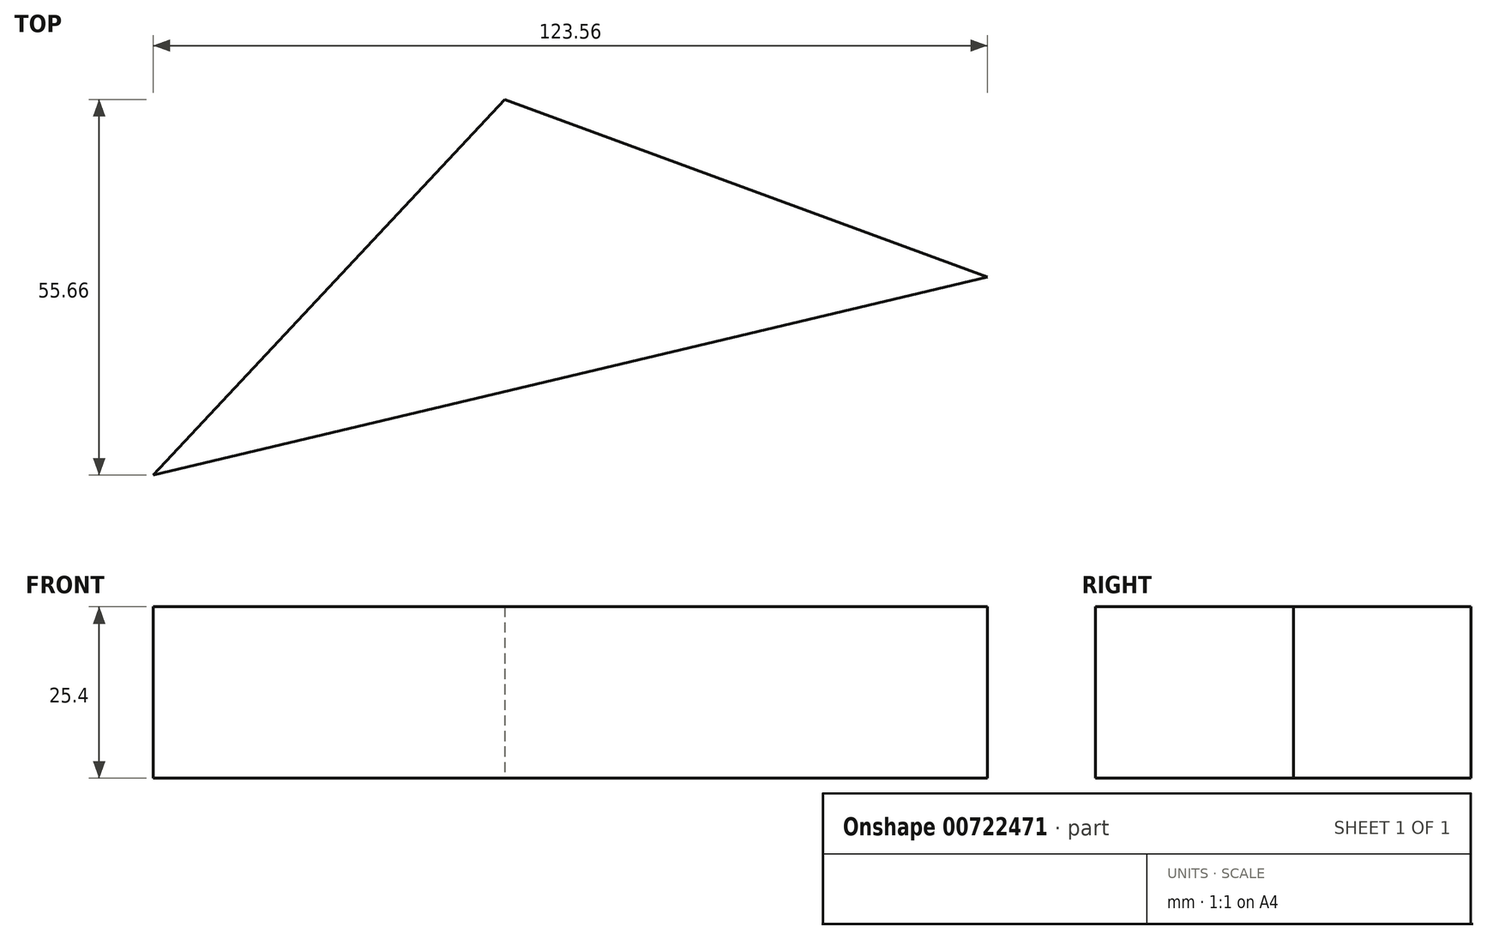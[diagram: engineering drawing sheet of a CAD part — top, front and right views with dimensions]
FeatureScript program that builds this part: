
annotation { "Feature Type Name" : "Feature", "Feature Type Description" : "" }
export const myFeature = defineFeature(function(context is Context, id is Id, definition is map)
    precondition{}
    {
        {
            var Q0;
            Q0=qCreatedBy(makeId("Top.planeOp"),FACE);
            var sketch = newSketch(context, id + "F0", { "sketchPlane" : qUnion([Q0])});
            skLineSegment(sketch, "E0", {"start": v(-52.05, 51.16) * mm, "end": v(71.51, 80.5) * mm});
            skLineSegment(sketch, "E1", {"start": v(71.51, 80.5) * mm, "end": v(0, 106.82) * mm});
            skLineSegment(sketch, "E2", {"start": v(0, 106.82) * mm, "end": v(-52.05, 51.16) * mm});
            skSolve(sketch);
        }
        {
            var Q0;
            Q0 = qSketchRegion(id + "F0", true);
            extrude(context, id + "F1", {"entities" : qUnion([Q0]), "depth" : 25.4 * mm, "offsetDistance" : 25.4 * mm});
        }
    });
